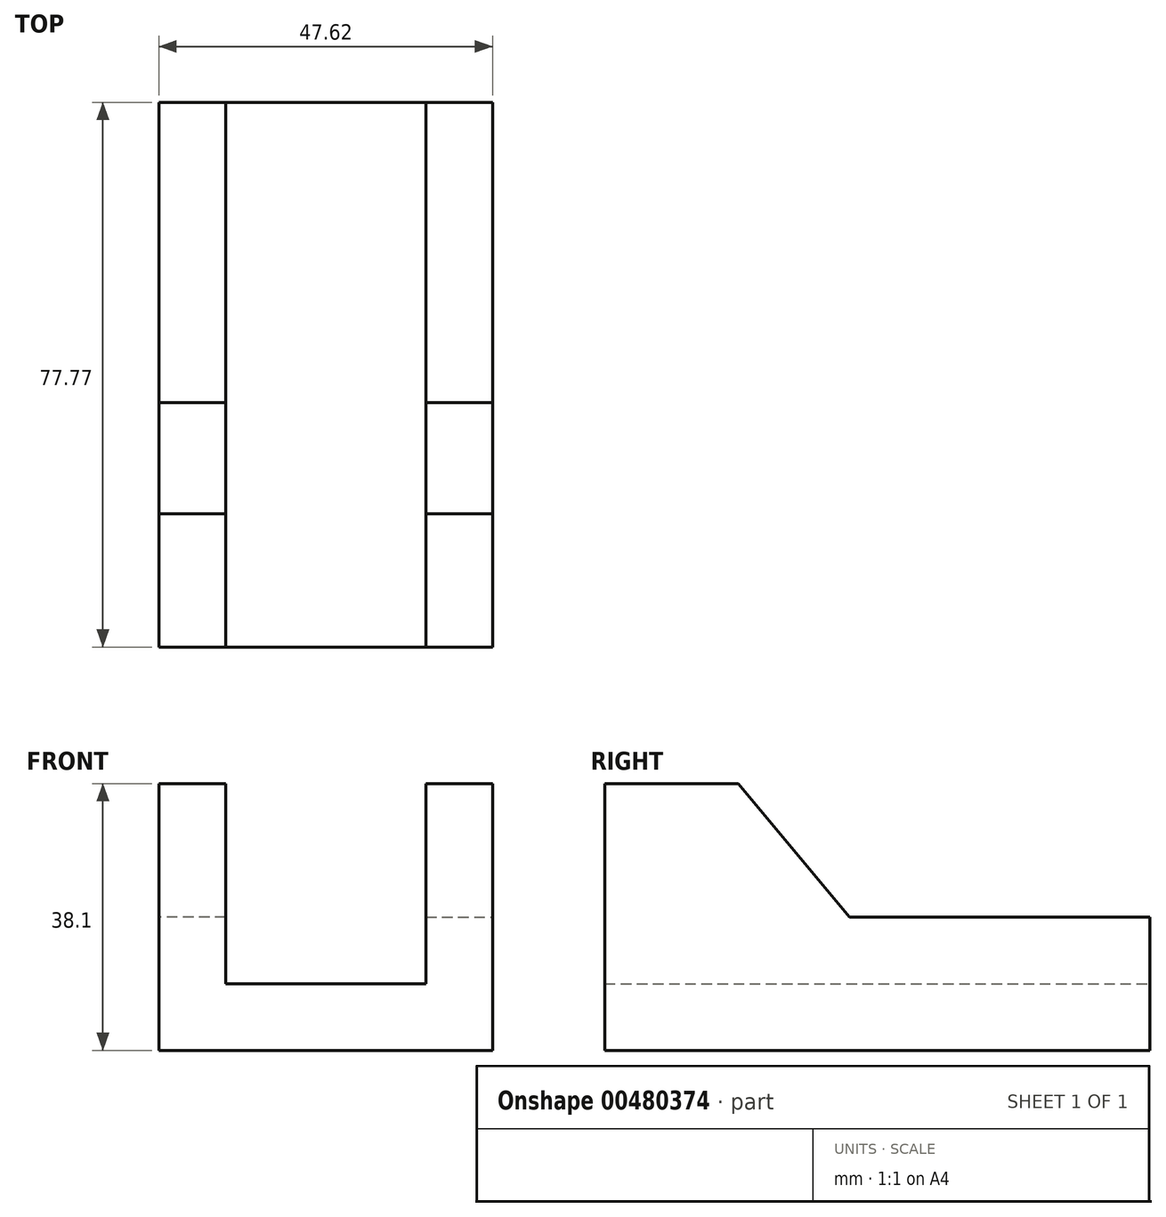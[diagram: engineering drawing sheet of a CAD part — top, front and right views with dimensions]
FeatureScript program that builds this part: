
annotation { "Feature Type Name" : "Feature", "Feature Type Description" : "" }
export const myFeature = defineFeature(function(context is Context, id is Id, definition is map)
    precondition{}
    {
        {
            var Q0;
            Q0=qCreatedBy(makeId("Right.planeOp"),FACE);
            var sketch = newSketch(context, id + "F0", { "sketchPlane" : qUnion([Q0])});
            skLineSegment(sketch, "E0", {"start": v(-77.77, 0) * mm, "end": v(-77.77, 38.1) * mm});
            skLineSegment(sketch, "E1", {"start": v(-77.77, 38.1) * mm, "end": v(-58.72, 38.1) * mm});
            skLineSegment(sketch, "E2", {"start": v(-58.72, 38.1) * mm, "end": v(-42.85, 19.05) * mm});
            skLineSegment(sketch, "E3", {"start": v(-42.85, 19.05) * mm, "end": v(0, 19.05) * mm});
            skLineSegment(sketch, "E4", {"start": v(0, 19.05) * mm, "end": v(0, 0) * mm});
            skLineSegment(sketch, "E5", {"start": v(0, 0) * mm, "end": v(-77.77, 0) * mm});
            skLineSegment(sketch, "E6", {"start": v(-77.77, 9.52) * mm, "end": v(0, 9.53) * mm});
            skSolve(sketch);
        }
        {
            var Q0;
            {var subQ0=sQuery(id+"F0.wireOp",EDGE,"E5");Q0=makeQuery(id+"F0.imprint","IMPRINT",FACE,{"disambiguationData":[TD([[makeQuery(id+"F0.imprint","IMPRINT",EDGE,{"derivedFrom":subQ0}),-1.0]])]});}
            extrude(context, id + "F1", {"entities" : qUnion([Q0]), "depth" : 23.8 * mm});
        }
        {
            var Q0;
            Q0 = qSketchRegion(id + "F0", true);
            extrude(context, id + "F2", {"entities" : qUnion([Q0]), "operationType" : NewBodyOperationType.ADD, "depth" : 9.52 * mm});
        }
        {
            var Q0;
            Q0=makeQuery(id+"F1.opExtrude","SWEPT_BODY",BODY,{"disambiguationData":[OSD([sQuery(id+"F0.wireOp",EDGE,"E0"),sQuery(id+"F0.wireOp",EDGE,"E4"),sQuery(id+"F0.wireOp",EDGE,"E5"),sQuery(id+"F0.wireOp",EDGE,"E6")])]});
            var Q1;
            Q1=makeQuery(id+"F1.opExtrude","CAP_FACE",FACE,{"disambiguationData":[OSD([sQuery(id+"F0.wireOp",EDGE,"E0"),sQuery(id+"F0.wireOp",EDGE,"E4"),sQuery(id+"F0.wireOp",EDGE,"E5"),sQuery(id+"F0.wireOp",EDGE,"E6")])],"isStart":false});
            mirror(context, id + "F3", {"operationType" : NewBodyOperationType.ADD, "entities" : qUnion([Q0]), "mirrorPlane" : qUnion([Q1])});
        }
    });
